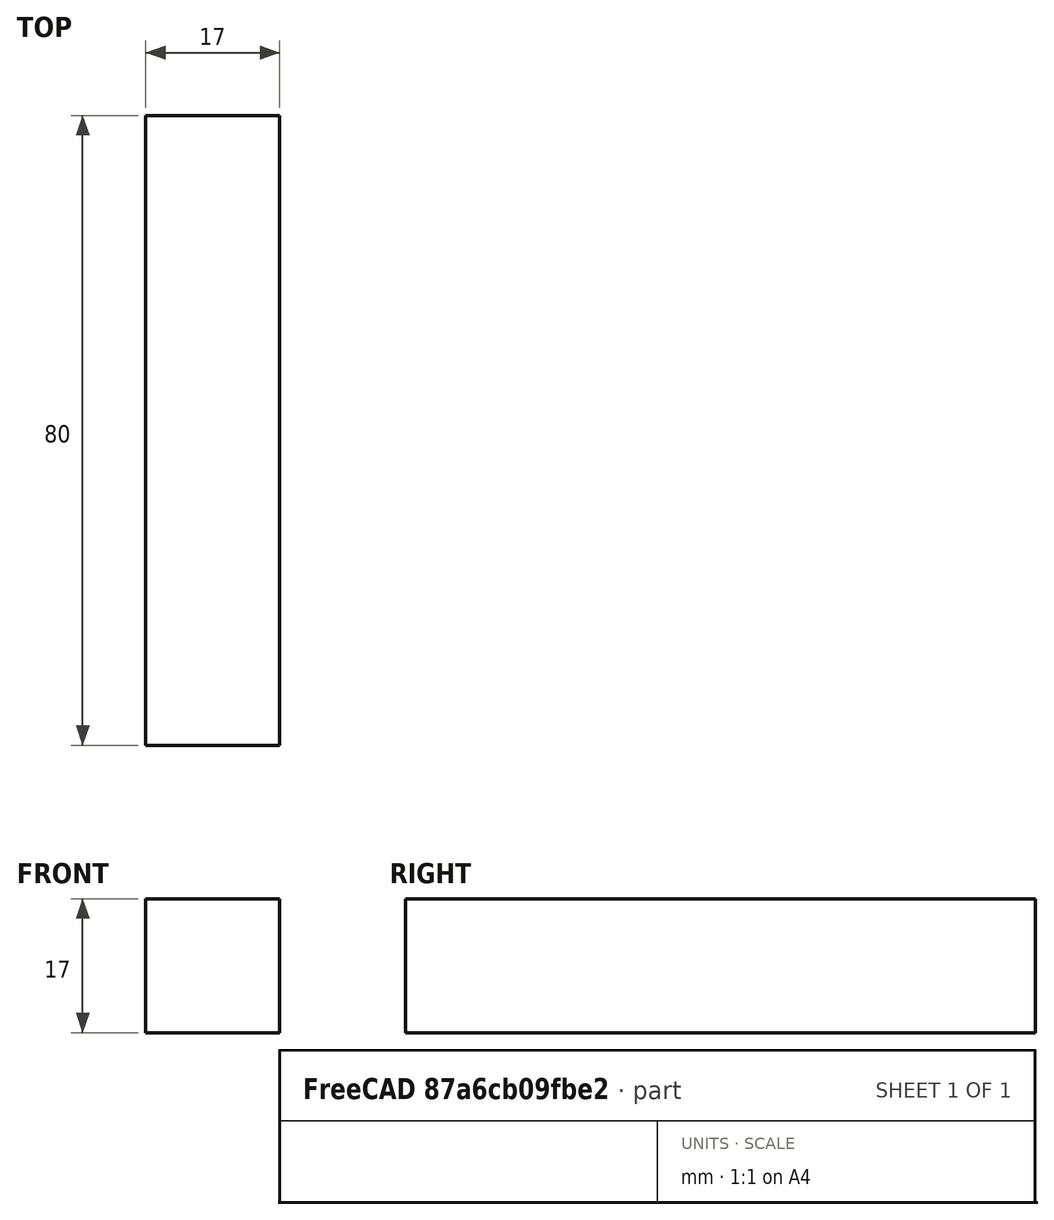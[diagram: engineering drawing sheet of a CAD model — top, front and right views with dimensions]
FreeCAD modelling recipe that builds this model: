
FCSTD DOCUMENT  (FreeCAD 0.15R4671 (Git))
Label: connector_no_drill
License: All rights reserved
LicenseURL: http://en.wikipedia.org/wiki/All_rights_reserved
objects: Sketcher::SketchObject×1, PartDesign::Pad×1
note: 3 computed .brp shape members not serialized (recipe doc carries the construction recipe); baked Part::Feature solids carry a one-line shape summary decoded from their .brp

FEATURE [Sketcher::SketchObject] Sketch
  sketch-geometry (4):
    g0: LineSegment StartX=0 StartY=80 StartZ=0 EndX=17 EndY=80 EndZ=0
    g1: LineSegment StartX=17 StartY=80 StartZ=0 EndX=17 EndY=0 EndZ=0
    g2: LineSegment StartX=17 StartY=0 StartZ=0 EndX=0 EndY=0 EndZ=0
    g3: LineSegment StartX=0 StartY=0 StartZ=0 EndX=0 EndY=80 EndZ=0
  constraints (11):
    c: Coincident(g0,g1)
    c: Coincident(g1,g2)
    c: Coincident(g2,g3)
    c: Coincident(g3,g0)
    c: Horizontal(g0)
    c: Horizontal(g2)
    c: Vertical(g1)
    c: Vertical(g3)
    c: Coincident(g2,g-1)
    c: DistanceX(g0) = 17
    c: DistanceY(g1) = -80
FEATURE [PartDesign::Pad] Pad
  Length = 17
  Length2 = 100
  Sketch = -> Sketch
  Type = 0
